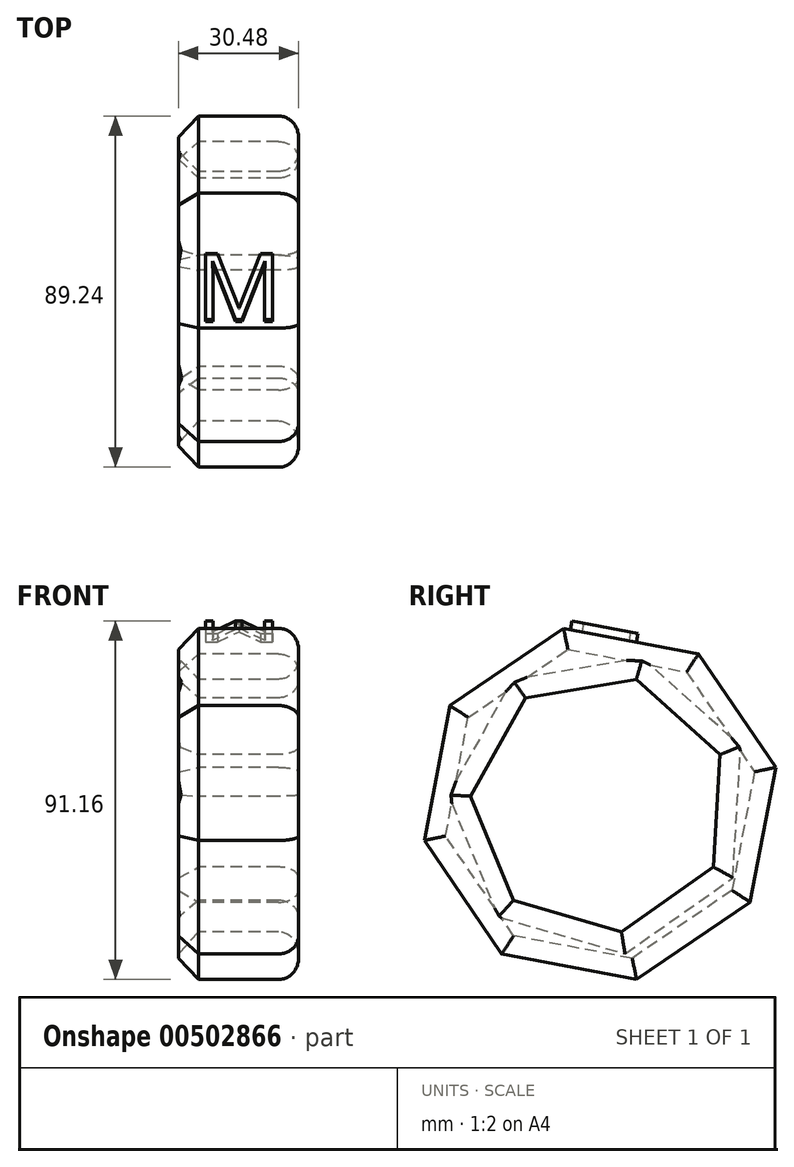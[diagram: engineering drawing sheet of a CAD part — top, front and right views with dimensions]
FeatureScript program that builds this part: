
annotation { "Feature Type Name" : "Feature", "Feature Type Description" : "" }
export const myFeature = defineFeature(function(context is Context, id is Id, definition is map)
    precondition{}
    {
        {
            var Q0;
            Q0=qCreatedBy(makeId("Right.planeOp"),FACE);
            var sketch = newSketch(context, id + "F0", { "sketchPlane" : qUnion([Q0])});
            skCircle(sketch, "E0.cCircle", {"center": v(0, 0) * mm, "radius": 42.1 * mm, "construction": true});
            skLineSegment(sketch, "E0.0", {"start": v(38.12, -25) * mm, "end": v(9.28, -44.62) * mm});
            skLineSegment(sketch, "E0.1", {"start": v(9.28, -44.62) * mm, "end": v(-25, -38.12) * mm});
            skLineSegment(sketch, "E0.2", {"start": v(-25, -38.12) * mm, "end": v(-44.62, -9.28) * mm});
            skLineSegment(sketch, "E0.3", {"start": v(-44.62, -9.28) * mm, "end": v(-38.12, 25) * mm});
            skLineSegment(sketch, "E0.4", {"start": v(-38.12, 25) * mm, "end": v(-9.28, 44.62) * mm});
            skLineSegment(sketch, "E0.5", {"start": v(-9.28, 44.62) * mm, "end": v(25, 38.12) * mm});
            skLineSegment(sketch, "E0.6", {"start": v(25, 38.12) * mm, "end": v(44.62, 9.28) * mm});
            skLineSegment(sketch, "E0.7", {"start": v(44.62, 9.28) * mm, "end": v(38.12, -25) * mm});
            skPoint(sketch, "E0.0.midPoint", {"position": v(23.7, -34.8) * mm});
            skSolve(sketch);
        }
        {
            var Q0;
            Q0=makeQuery(id+"F0.imprint","IMPRINT",FACE,{"disambiguationData":[TD([[makeQuery(id+"F0.imprint","IMPRINT",EDGE,{"derivedFrom":sQuery(id+"F0.wireOp",EDGE,"E0.0")}),-1.0]])]});
            extrude(context, id + "F1", {"entities" : qUnion([Q0]), "depth" : 30.48 * mm});
        }
        {
            var Q0;
            Q0=makeQuery(id+"F1.opExtrude","CAP_FACE",FACE,{"disambiguationData":[OSD([sQuery(id+"F0.wireOp",EDGE,"E0.0"),sQuery(id+"F0.wireOp",EDGE,"E0.1"),sQuery(id+"F0.wireOp",EDGE,"E0.2"),sQuery(id+"F0.wireOp",EDGE,"E0.3"),sQuery(id+"F0.wireOp",EDGE,"E0.4"),sQuery(id+"F0.wireOp",EDGE,"E0.5"),sQuery(id+"F0.wireOp",EDGE,"E0.6"),sQuery(id+"F0.wireOp",EDGE,"E0.7")])],"isStart":true});
            var sketch = newSketch(context, id + "F2", { "sketchPlane" : qUnion([Q0])});
            skCircle(sketch, "E1.cCircle", {"center": v(0, 0) * mm, "radius": 29.72 * mm, "construction": true});
            skLineSegment(sketch, "E1.0", {"start": v(19, 26.96) * mm, "end": v(32.93, 1.95) * mm});
            skLineSegment(sketch, "E1.1", {"start": v(32.93, 1.95) * mm, "end": v(22.05, -24.53) * mm});
            skLineSegment(sketch, "E1.2", {"start": v(22.05, -24.53) * mm, "end": v(-5.43, -32.53) * mm});
            skLineSegment(sketch, "E1.3", {"start": v(-5.43, -32.53) * mm, "end": v(-28.82, -16.04) * mm});
            skLineSegment(sketch, "E1.4", {"start": v(-28.82, -16.04) * mm, "end": v(-30.51, 12.53) * mm});
            skLineSegment(sketch, "E1.5", {"start": v(-30.51, 12.53) * mm, "end": v(-9.23, 31.67) * mm});
            skLineSegment(sketch, "E1.6", {"start": v(-9.23, 31.67) * mm, "end": v(19, 26.96) * mm});
            skPoint(sketch, "E1.0.midPoint", {"position": v(25.97, 14.45) * mm});
            skSolve(sketch);
        }
        {
            var Q0;
            Q0 = qSketchRegion(id + "F2", true);
            extrude(context, id + "F3", {"entities" : qUnion([Q0]), "operationType" : NewBodyOperationType.REMOVE, "oppositeDirection" : true, "depth" : 60.2 * mm});
        }
        {
            var Q0;
            Q0=makeQuery(id+"F1.opExtrude","CAP_FACE",FACE,{"disambiguationData":[OSD([sQuery(id+"F0.wireOp",EDGE,"E0.0"),sQuery(id+"F0.wireOp",EDGE,"E0.1"),sQuery(id+"F0.wireOp",EDGE,"E0.2"),sQuery(id+"F0.wireOp",EDGE,"E0.3"),sQuery(id+"F0.wireOp",EDGE,"E0.4"),sQuery(id+"F0.wireOp",EDGE,"E0.5"),sQuery(id+"F0.wireOp",EDGE,"E0.6"),sQuery(id+"F0.wireOp",EDGE,"E0.7")])],"isStart":false});
            fillet(context, id + "F4", {"entities" : qUnion([Q0]), "radius" : 5.08 * mm, "tangentPropagation" : true, "allowEdgeOverflow" : false});
        }
        {
            var Q0;
            Q0=makeQuery(id+"F1.opExtrude","CAP_FACE",FACE,{"disambiguationData":[OSD([sQuery(id+"F0.wireOp",EDGE,"E0.0"),sQuery(id+"F0.wireOp",EDGE,"E0.1"),sQuery(id+"F0.wireOp",EDGE,"E0.2"),sQuery(id+"F0.wireOp",EDGE,"E0.3"),sQuery(id+"F0.wireOp",EDGE,"E0.4"),sQuery(id+"F0.wireOp",EDGE,"E0.5"),sQuery(id+"F0.wireOp",EDGE,"E0.6"),sQuery(id+"F0.wireOp",EDGE,"E0.7")])],"isStart":true});
            chamfer(context, id + "F5", {"entities" : qUnion([Q0]), "width" : 5.08 * mm, "tangentPropagation" : true});
        }
        {
            var Q0;
            Q0=makeQuery(id+"F1.opExtrude","SWEPT_FACE",FACE,{"disambiguationData":[OSD([sQuery(id+"F0.wireOp",EDGE,"E0.5")])]});
            var sketch = newSketch(context, id + "F6", { "sketchPlane" : qUnion([Q0])});
            skText(sketch, "E2", { "text": "M", "fontName": "OpenSans-Regular.ttf"});
            const initialGuessF6  = {"E2": [0.00458, -0.01568, 1, 0, 0.01723]};
            skSetInitialGuess(sketch, initialGuessF6);
            skSolve(sketch);
        }
        {
            var Q0;
            Q0 = qSketchRegion(id + "F6", true);
            extrude(context, id + "F7", {"entities" : qUnion([Q0]), "operationType" : NewBodyOperationType.ADD, "depth" : 2.3 * mm});
        }
    });
